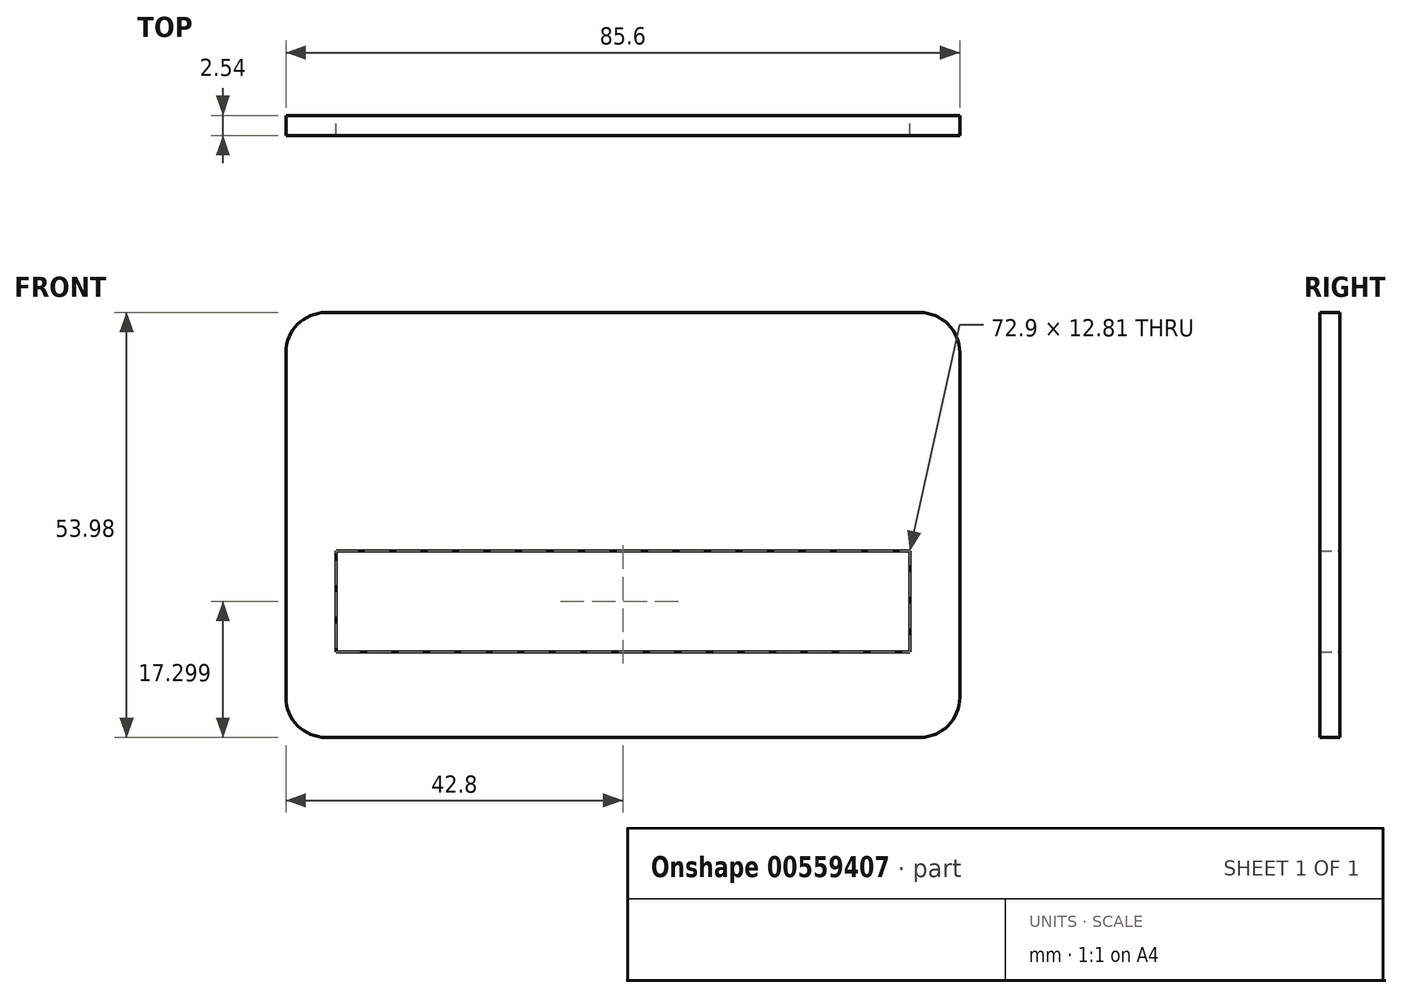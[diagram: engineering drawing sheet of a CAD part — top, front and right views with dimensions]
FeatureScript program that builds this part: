
annotation { "Feature Type Name" : "Feature", "Feature Type Description" : "" }
export const myFeature = defineFeature(function(context is Context, id is Id, definition is map)
    precondition{}
    {
        {
            var Q0;
            Q0=qCreatedBy(makeId("Front.planeOp"),FACE);
            var sketch = newSketch(context, id + "F0", { "sketchPlane" : qUnion([Q0])});
            skLineSegment(sketch, "E0.bottom", {"start": v(-37.72, 26.99) * mm, "end": v(37.72, 26.99) * mm});
            skLineSegment(sketch, "E0.top", {"start": v(-37.72, -26.99) * mm, "end": v(37.72, -26.99) * mm});
            skLineSegment(sketch, "E0.left", {"start": v(-42.8, 21.9) * mm, "end": v(-42.8, -21.9) * mm});
            skLineSegment(sketch, "E0.right", {"start": v(42.8, 21.9) * mm, "end": v(42.8, -21.9) * mm});
            skPoint(sketch, "E0.middle", {"position": v(0, 0) * mm});
            skPoint(sketch, "E1.visualSharp", {"position": v(-42.8, 26.99) * mm});
            skArc(sketch, "E1.filletArc", {"start": v(-37.72, 26.99) * mm, "mid": v(-41.31, 25.5) * mm, "end": v(-42.8, 21.9) * mm});
            skPoint(sketch, "E2.visualSharp", {"position": v(42.8, 26.99) * mm});
            skArc(sketch, "E2.filletArc", {"start": v(42.8, 21.9) * mm, "mid": v(41.31, 25.5) * mm, "end": v(37.72, 26.99) * mm});
            skPoint(sketch, "E3.visualSharp", {"position": v(-42.8, -26.99) * mm});
            skArc(sketch, "E3.filletArc", {"start": v(-42.8, -21.9) * mm, "mid": v(-41.31, -25.5) * mm, "end": v(-37.72, -26.99) * mm});
            skPoint(sketch, "E4.visualSharp", {"position": v(42.8, -26.99) * mm});
            skArc(sketch, "E4.filletArc", {"start": v(37.72, -26.99) * mm, "mid": v(41.31, -25.5) * mm, "end": v(42.8, -21.9) * mm});
            skLineSegment(sketch, "E5.bottom", {"start": v(-36.45, -16.1) * mm, "end": v(36.45, -16.1) * mm});
            skLineSegment(sketch, "E5.top", {"start": v(-36.45, -3.29) * mm, "end": v(36.45, -3.29) * mm});
            skLineSegment(sketch, "E5.left", {"start": v(-36.45, -16.1) * mm, "end": v(-36.45, -3.29) * mm});
            skLineSegment(sketch, "E5.right", {"start": v(36.45, -16.1) * mm, "end": v(36.45, -3.29) * mm});
            skPoint(sketch, "E5.middle", {"position": v(0, -9.7) * mm});
            skSolve(sketch);
        }
        {
            var Q0;
            Q0=makeQuery(id+"F0.imprint","IMPRINT",FACE,{"disambiguationData":[TD([[makeQuery(id+"F0.imprint","IMPRINT",EDGE,{"derivedFrom":sQuery(id+"F0.wireOp",EDGE,"E0.bottom")}),-1.0]])]});
            extrude(context, id + "F1", {"entities" : qUnion([Q0]), "depth" : 2.54 * mm, "offsetDistance" : 25.4 * mm});
        }
    });
